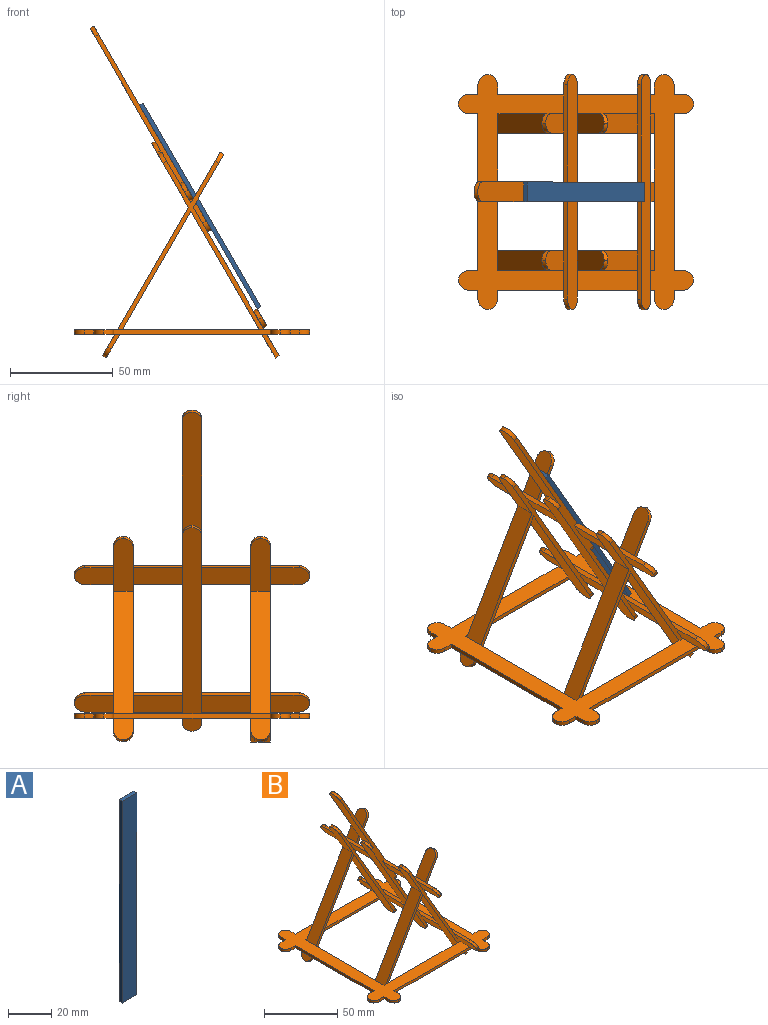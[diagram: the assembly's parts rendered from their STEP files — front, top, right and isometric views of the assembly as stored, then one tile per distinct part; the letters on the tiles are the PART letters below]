
ASSEMBLY  parts=2 mates=1
PART A: 6 faces, bbox 9.5x2.1x114.3 mm
  f0: plane 114.3x2.11mm, normal (-1,0,0), area 241mm2, adj f1,f3,f4,f5
  f1: plane 9.53x2.11mm, normal (0,0,-1), area 20.1mm2, adj f0,f2,f4,f5
  f2: plane 114.3x2.11mm, normal (1,0,0), area 241mm2, adj f1,f3,f4,f5
  f3: plane 9.53x2.11mm, normal (0,0,1), area 20.1mm2, adj f0,f2,f4,f5
  f4: plane 114.3x9.53mm, normal (0,-1,0), area 1088.7mm2, adj f0,f1,f2,f3
  f5: plane 114.3x9.53mm, normal (0,1,0), area 1088.7mm2, adj f0,f1,f2,f3
PART B: 126 faces, bbox 114.3x114.3x161.3 mm
  f0: plane 42.61x24.6mm, normal (0.87,0,0.5), area 433mm2, adj f74,f78,f79,f125
  f1: plane 47.31x1.83mm, normal (-0.5,0,0.87), area 99.7mm2, adj f3,f67,f68,f71,f79,f90
  f2: plane 47.31x1.83mm, normal (0.5,0,-0.87), area 99.6mm2, adj f3,f10,f14,f15,f16,f68,f71,f79
  f3: plane 23.81x8.25mm, normal (-0.87,0,-0.5), area 226.8mm2, adj f1,f2,f15,f79
  f4: plane 23.81x8.25mm, normal (-0.87,0,-0.5), area 226.8mm2, adj f12,f69,f70,f78
  f5: plane 23.81x8.25mm, normal (-0.87,0,-0.5), area 226.8mm2, adj f15,f74,f75,f79
  f6: plane 23.81x8.25mm, normal (-0.87,0,-0.5), area 226.8mm2, adj f12,f74,f75,f78
  f7: plane 50.49x29.15mm, normal (0.87,0,0.5), area 555.4mm2, adj f12,f13,f54,f74
  f8: plane 13.49x9.53mm, normal (0.87,0,0.5), area 137.4mm2, adj f15,f16,f17,f59,f75,f94,f95
  f9: plane 15.33x9.53mm, normal (0.87,0,0.5), area 157.7mm2, adj f12,f13,f69,f104,f105
  f10: plane 9.53x1.05mm, normal (0.87,0,0.5), area 11.5mm2, adj f2,f14,f15,f16
  f11: plane 9.53x2.09mm, normal (-0.87,0,0.5), area 23mm2, adj f12,f13,f52,f70
  f12: plane 95.64x83.31mm, normal (0,1,0), area 444.7mm2, adj f4,f6,f7,f9,f11,f49,f50,f51
  f13: plane 81.99x71.3mm, normal (0,-1,0), area 391.5mm2, adj f7,f9,f11,f45,f49,f50,f51,f52
  f14: plane 9.53x2.09mm, normal (-0.87,0,0.5), area 23mm2, adj f2,f10,f15,f16
  f15: plane 91.24x80.77mm, normal (0,-1,0), area 434mm2, adj f2,f3,f5,f8,f10,f14,f60,f61
  f16: plane 81.99x71.3mm, normal (0,1,0), area 391.5mm2, adj f2,f8,f10,f14,f45,f60,f61,f62
  f17: plane 3x2.11mm, normal (0,-1,0), area 5.1mm2, adj f8,f43,f45,f46
  f18: plane 68.87x2.11mm, normal (0,-1,0), area 142.6mm2, adj f45,f46,f62,f63
  f19: plane 68.87x2.11mm, normal (0,1,0), area 142.6mm2, adj f45,f46,f49,f57
  f20: plane 2.11x1.89mm, normal (0,1,0), area 2.7mm2, adj f41,f45,f46,f50
  f21: plane 4.45x2.11mm, normal (0,-1,0), area 9.4mm2, adj f22,f45,f46,f108
  f22: plane 76.2x2.11mm, normal (-1,0,0), area 160.6mm2, adj f21,f23,f45,f46
  f23: plane 4.45x2.11mm, normal (0,1,0), area 9.4mm2, adj f22,f45,f46,f121
  f24: plane 4.45x2.11mm, normal (0,-1,0), area 9.4mm2, adj f25,f45,f46,f120
  f25: plane 4.45x2.11mm, normal (-1,0,0), area 9.4mm2, adj f24,f45,f46,f119
  f26: plane 4.45x2.11mm, normal (1,0,0), area 9.4mm2, adj f27,f45,f46,f118
  f27: plane 76.2x2.11mm, normal (0,-1,0), area 160.6mm2, adj f26,f28,f45,f46
  f28: plane 4.45x2.11mm, normal (-1,0,0), area 9.4mm2, adj f27,f45,f46,f116
  f29: plane 4.45x2.11mm, normal (1,0,0), area 9.4mm2, adj f30,f45,f46,f117
  f30: plane 4.45x2.11mm, normal (0,-1,0), area 9.4mm2, adj f29,f45,f46,f115
  f31: plane 4.45x2.11mm, normal (0,1,0), area 9.4mm2, adj f32,f45,f46,f114
  f32: plane 76.2x2.11mm, normal (1,0,0), area 160.6mm2, adj f31,f33,f45,f46
  f33: plane 4.45x2.11mm, normal (0,-1,0), area 9.4mm2, adj f32,f45,f46,f113
  f34: plane 4.45x2.11mm, normal (0,1,0), area 9.4mm2, adj f35,f45,f46,f112
  f35: plane 4.45x2.11mm, normal (1,0,0), area 9.4mm2, adj f34,f45,f46,f111
  f36: plane 4.45x2.11mm, normal (-1,0,0), area 9.4mm2, adj f37,f45,f46,f110
  f37: plane 76.2x2.11mm, normal (0,1,0), area 160.6mm2, adj f36,f38,f45,f46
  f38: plane 4.45x2.11mm, normal (1,0,0), area 9.4mm2, adj f37,f45,f46,f107
  f39: plane 4.45x2.11mm, normal (-1,0,0), area 9.4mm2, adj f40,f45,f46,f106
  f40: plane 4.45x2.11mm, normal (0,1,0), area 9.4mm2, adj f39,f45,f46,f109
  f41: plane 76.2x2.11mm, normal (1,0,0), area 160.6mm2, adj f20,f42,f45,f46
  f42: plane 2.11x1.89mm, normal (0,-1,0), area 2.7mm2, adj f41,f45,f46,f61
  f43: plane 76.2x2.11mm, normal (-1,0,0), area 160.6mm2, adj f17,f44,f45,f46
  f44: plane 3x2.11mm, normal (0,1,0), area 5.1mm2, adj f43,f45,f46,f55
  f45: plane 114.28x114.28mm, normal (0,0,1), area 3903.3mm2, adj f13,f16,f17,f18,f19,f20,f21,f22
  f46: plane 114.28x114.28mm, normal (0,0,-1), area 3903.3mm2, adj f17,f18,f19,f20,f21,f22,f23,f24
  f47: plane 11.55x8.49mm, normal (0,-1,0), area 26.8mm2, adj f46,f55,f56,f57
  f48: plane 7.15x5.95mm, normal (0,-1,0), area 16.1mm2, adj f46,f49,f50,f101
  f49: plane 71.18x41.1mm, normal (0.87,0,-0.5), area 771.9mm2, adj f12,f13,f19,f48,f57,f100,f101
  f50: plane 72.23x41.7mm, normal (-0.87,0,0.5), area 783.5mm2, adj f12,f13,f20,f48,f51,f100,f101
  f51: plane 25.68x14.83mm, normal (-0.87,0,-0.5), area 271.5mm2, adj f12,f13,f50,f104,f105
  f52: plane 9.53x1.05mm, normal (0.87,0,0.5), area 11.5mm2, adj f11,f12,f13,f70
  f53: plane 22.52x13mm, normal (-0.87,0,0.5), area 236.7mm2, adj f12,f13,f71,f102,f103
  f54: plane 25.68x14.83mm, normal (0.87,0,-0.5), area 271.5mm2, adj f7,f12,f13,f102,f103
  f55: plane 13.5x9.53mm, normal (0.87,0,0.5), area 148.5mm2, adj f12,f13,f44,f47,f56,f75
  f56: plane 9.53x1.83mm, normal (0.5,0,-0.87), area 20.1mm2, adj f12,f47,f55,f57
  f57: plane 71.19x41.1mm, normal (-0.87,0,-0.5), area 783mm2, adj f12,f13,f19,f47,f49,f56
  f58: plane 7.15x5.95mm, normal (0,1,0), area 16.1mm2, adj f46,f61,f62,f93
  f59: plane 7.15x5.95mm, normal (0,1,0), area 16.1mm2, adj f8,f46,f63,f95
  f60: plane 25.68x14.83mm, normal (-0.87,0,-0.5), area 271.5mm2, adj f15,f16,f61,f98,f99
  f61: plane 72.23x41.7mm, normal (-0.87,0,0.5), area 783.5mm2, adj f15,f16,f42,f58,f60,f92,f93
  f62: plane 71.18x41.1mm, normal (0.87,0,-0.5), area 771.9mm2, adj f15,f16,f18,f58,f63,f92,f93
  f63: plane 71.18x41.1mm, normal (-0.87,0,-0.5), area 771.9mm2, adj f15,f16,f18,f59,f62,f94,f95
  f64: plane 50.49x29.15mm, normal (0.87,0,0.5), area 555.4mm2, adj f15,f16,f65,f74
  f65: plane 25.68x14.83mm, normal (0.87,0,-0.5), area 271.5mm2, adj f15,f16,f64,f96,f97
  f66: plane 22.52x13mm, normal (-0.87,0,0.5), area 236.7mm2, adj f15,f16,f71,f96,f97
  f67: plane 15.33x9.53mm, normal (0.87,0,0.5), area 157.7mm2, adj f1,f15,f16,f98,f99
  f68: plane 19.04x8.25mm, normal (-0.87,0,-0.5), area 170.4mm2, adj f1,f2,f16,f90,f91
  f69: plane 47.31x1.83mm, normal (-0.5,0,0.87), area 99.7mm2, adj f4,f9,f71,f72,f78,f89
  f70: plane 47.31x1.83mm, normal (0.5,0,-0.87), area 99.6mm2, adj f4,f11,f12,f13,f52,f71,f72,f78
  f71: plane 114.28x98.99mm, normal (0.87,0,0.5), area 2044.9mm2, adj f1,f2,f12,f13,f15,f16,f53,f66
  f72: plane 19.04x8.25mm, normal (-0.87,0,-0.5), area 170.4mm2, adj f13,f69,f70,f88,f89
  f73: plane 19.04x8.25mm, normal (-0.87,0,-0.5), area 170.4mm2, adj f16,f74,f75,f86,f87
  f74: plane 104.14x1.83mm, normal (-0.5,0,0.87), area 219.5mm2, adj f0,f5,f6,f7,f64,f73,f76,f77
  f75: plane 104.14x1.83mm, normal (0.5,0,-0.87), area 219.5mm2, adj f5,f6,f8,f55,f73,f76,f77,f81
  f76: plane 114.28x8.25mm, normal (0.87,0,0.5), area 1066.6mm2, adj f74,f75,f84,f85,f86,f87
  f77: plane 19.04x8.25mm, normal (-0.87,0,-0.5), area 170.4mm2, adj f13,f74,f75,f84,f85
  f78: plane 147.83x84.13mm, normal (0,-1,0), area 421mm2, adj f0,f4,f6,f69,f70,f71,f80,f81
  f79: plane 147.83x84.13mm, normal (0,1,0), area 421mm2, adj f0,f1,f2,f3,f5,f71,f80,f81
  f80: plane 98.98x57.15mm, normal (-0.87,0,-0.5), area 1067.9mm2, adj f78,f79,f82,f83,f122
  f81: plane 9.53x8.25mm, normal (0.87,0,0.5), area 81mm2, adj f75,f78,f79,f122
  f82: cylinder r=5.08mm len=5.45mm, axis (-0.87,0,-0.5), area 16.2mm2, adj f79,f80,f83,f123
  f83: cylinder r=5.08mm len=5.45mm, axis (-0.87,0,-0.5), area 16.2mm2, adj f78,f80,f82,f123
  f84: cylinder r=5.08mm len=5.18mm, axis (-0.87,0,-0.5), area 16.2mm2, adj f75,f76,f77,f85
  f85: cylinder r=5.08mm len=5.18mm, axis (0.87,0,0.5), area 16.2mm2, adj f74,f76,f77,f84
  f86: cylinder r=5.08mm len=5.18mm, axis (-0.87,0,-0.5), area 16.2mm2, adj f73,f74,f76,f87
  f87: cylinder r=5.08mm len=5.18mm, axis (0.87,0,0.5), area 16.2mm2, adj f73,f75,f76,f86
  f88: cylinder r=5.08mm len=5.18mm, axis (-0.87,0,-0.5), area 16.2mm2, adj f70,f71,f72,f89
  f89: cylinder r=5.08mm len=5.18mm, axis (0.87,0,0.5), area 16.2mm2, adj f69,f71,f72,f88
  f90: cylinder r=5.08mm len=5.18mm, axis (-0.87,0,-0.5), area 16.2mm2, adj f1,f68,f71,f91
  f91: cylinder r=5.08mm len=5.18mm, axis (0.87,0,0.5), area 16.2mm2, adj f2,f68,f71,f90
  f92: cylinder r=5.08mm len=5.45mm, axis (-0.87,0,0.5), area 16.2mm2, adj f15,f61,f62,f93
  f93: cylinder r=5.08mm len=5.45mm, axis (0.87,0,-0.5), area 16.2mm2, adj f58,f61,f62,f92
  f94: cylinder r=5.08mm len=5.45mm, axis (-0.87,0,-0.5), area 16.2mm2, adj f8,f15,f63,f95
  f95: cylinder r=5.08mm len=5.45mm, axis (0.87,0,0.5), area 16.2mm2, adj f8,f59,f63,f94
  f96: cylinder r=5.08mm len=5.45mm, axis (0.87,0,-0.5), area 16.2mm2, adj f15,f65,f66,f97
  f97: cylinder r=5.08mm len=5.45mm, axis (-0.87,0,0.5), area 16.2mm2, adj f16,f65,f66,f96
  f98: cylinder r=5.08mm len=5.45mm, axis (0.87,0,0.5), area 16.2mm2, adj f15,f60,f67,f99
  f99: cylinder r=5.08mm len=5.45mm, axis (-0.87,0,-0.5), area 16.2mm2, adj f16,f60,f67,f98
  f100: cylinder r=5.08mm len=5.45mm, axis (0.87,0,-0.5), area 16.2mm2, adj f12,f49,f50,f101
  f101: cylinder r=5.08mm len=5.45mm, axis (-0.87,0,0.5), area 16.2mm2, adj f48,f49,f50,f100
  f102: cylinder r=5.08mm len=5.45mm, axis (-0.87,0,0.5), area 16.2mm2, adj f12,f53,f54,f103
  f103: cylinder r=5.08mm len=5.45mm, axis (0.87,0,-0.5), area 16.2mm2, adj f13,f53,f54,f102
  f104: cylinder r=5.08mm len=5.45mm, axis (-0.87,0,-0.5), area 16.2mm2, adj f9,f12,f51,f105
  f105: cylinder r=5.08mm len=5.45mm, axis (0.87,0,0.5), area 16.2mm2, adj f9,f13,f51,f104
  f106: cylinder r=5.08mm len=5.07mm, axis (0,0,1), area 16.2mm2, adj f39,f45,f46,f107
  f107: cylinder r=5.08mm len=5.07mm, axis (0,0,-1), area 16.2mm2, adj f38,f45,f46,f106
  f108: cylinder r=5.08mm len=5.07mm, axis (0,0,-1), area 16.2mm2, adj f21,f45,f46,f109
  f109: cylinder r=5.08mm len=5.07mm, axis (0,0,1), area 16.2mm2, adj f40,f45,f46,f108
  f110: cylinder r=5.08mm len=5.07mm, axis (0,0,1), area 16.2mm2, adj f36,f45,f46,f111
  f111: cylinder r=5.08mm len=5.07mm, axis (0,0,-1), area 16.2mm2, adj f35,f45,f46,f110
  f112: cylinder r=5.08mm len=5.07mm, axis (0,0,-1), area 16.2mm2, adj f34,f45,f46,f113
  f113: cylinder r=5.08mm len=5.07mm, axis (0,0,1), area 16.2mm2, adj f33,f45,f46,f112
  f114: cylinder r=5.08mm len=5.07mm, axis (0,0,-1), area 16.2mm2, adj f31,f45,f46,f115
  f115: cylinder r=5.08mm len=5.07mm, axis (0,0,1), area 16.2mm2, adj f30,f45,f46,f114
  f116: cylinder r=5.08mm len=5.07mm, axis (0,0,-1), area 16.2mm2, adj f28,f45,f46,f117
  f117: cylinder r=5.08mm len=5.07mm, axis (0,0,1), area 16.2mm2, adj f29,f45,f46,f116
  f118: cylinder r=5.08mm len=5.07mm, axis (0,0,1), area 16.2mm2, adj f26,f45,f46,f119
  f119: cylinder r=5.08mm len=5.07mm, axis (0,0,-1), area 16.2mm2, adj f25,f45,f46,f118
  f120: cylinder r=5.08mm len=5.07mm, axis (0,0,-1), area 16.2mm2, adj f24,f45,f46,f121
  f121: cylinder r=5.08mm len=5.07mm, axis (0,0,1), area 16.2mm2, adj f23,f45,f46,f120
  f122: cylinder r=4.76mm len=9.53mm, axis (0.87,0,0.5), area 31.5mm2, adj f78,f79,f80,f81
  f123: plane 59.38x34.29mm, normal (-0.87,0,-0.5), area 606.1mm2, adj f78,f79,f82,f83,f124
  f124: cylinder r=4.76mm len=9.53mm, axis (0.87,0,0.5), area 31.5mm2, adj f71,f78,f79,f123
  f125: cylinder r=4.76mm len=9.53mm, axis (-0.87,0,-0.5), area 31.5mm2, adj f0,f71,f78,f79
PLACE A rot(axis=(0.25,-0.25,-0.94),93.8deg) t=(-152.45,-40.81,103.04)mm
PLACE B t=(-135.69,-4.76,17.37)mm
MATE ball A.f4 <-> B.f76  axis (-0.87,0,-0.5) through (-112.53,-5.55,29.68)mm
